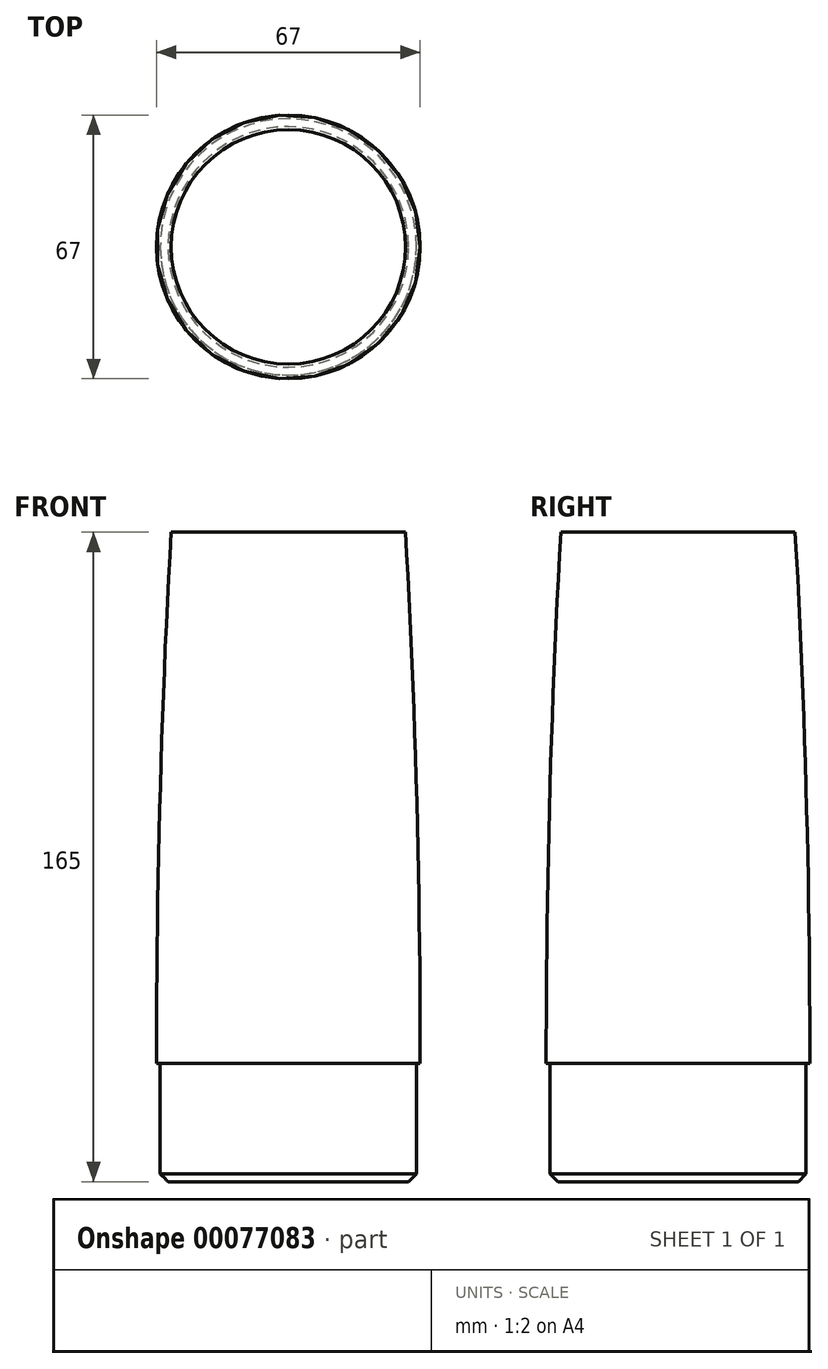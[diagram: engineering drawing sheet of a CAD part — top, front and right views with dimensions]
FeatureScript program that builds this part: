
annotation { "Feature Type Name" : "Feature", "Feature Type Description" : "" }
export const myFeature = defineFeature(function(context is Context, id is Id, definition is map)
    precondition{}
    {
        {
            var Q0;
            Q0=qCreatedBy(makeId("Front.planeOp"),FACE);
            var sketch = newSketch(context, id + "F0", { "sketchPlane" : qUnion([Q0])});
            skEllipticalArc(sketch, "E0", {});
            skLineSegment(sketch, "E1", {"start": v(0, 129) * mm, "end": v(0, -294) * mm, "construction": true});
            skPoint(sketch, "E1.endSnap0", {"position": v(0, 294) * mm});
            skLineSegment(sketch, "E2", {"start": v(-33.5, 0) * mm, "end": v(-32.55, 0) * mm, "construction": true});
            skPoint(sketch, "E2.endSnap0", {"position": v(33.5, 0) * mm});
            skPoint(sketch, "E3.orphan", {"position": v(0, 67.2) * mm});
            skPoint(sketch, "E4.orphan", {"position": v(0, -68.03) * mm});
            skLineSegment(sketch, "E5", {"start": v(-33.5, 0) * mm, "end": v(-32.55, 0) * mm});
            skLineSegment(sketch, "E6", {"start": v(-32.55, 0) * mm, "end": v(-32.55, -30) * mm});
            skLineSegment(sketch, "E7", {"start": v(-32.55, -30) * mm, "end": v(0, -30) * mm});
            skLineSegment(sketch, "E8", {"start": v(0, -30) * mm, "end": v(0, 294) * mm});
            skLineSegment(sketch, "E9.bottom", {"start": v(-32.55, 0) * mm, "end": v(-33.5, 0) * mm});
            skLineSegment(sketch, "E9.top", {"start": v(-25.6, 135) * mm, "end": v(-29.76, 135) * mm});
            skLineSegment(sketch, "E9.left", {"start": v(0, 0) * mm, "end": v(0, 129) * mm});
            skPoint(sketch, "E9.right.end.orphan", {"position": v(-47.64, 135) * mm});
            skPoint(sketch, "E10.orphan", {"position": v(-47.64, 0) * mm});
            skLineSegment(sketch, "E11.trimOffspring", {"start": v(0, 0) * mm, "end": v(40.39, 0) * mm, "construction": true});
            skPoint(sketch, "E12.orphan", {"position": v(-35.36, 0) * mm});
            skPoint(sketch, "E13.orphan", {"position": v(0, 135) * mm});
            skLineSegment(sketch, "E14", {"start": v(-25.6, 135) * mm, "end": v(0, 135) * mm});
            skPoint(sketch, "E15.right.end.orphan", {"position": v(-25.6, 129) * mm});
            const initialGuessF0  = {"E0": [0, 0, 0, 1, 0.294, 0.0335, 1.0937202801470427, 1.5707963267948966]};
            skSetInitialGuess(sketch, initialGuessF0);
            skSolve(sketch);
        }
        {
            var Q0;
            Q0=makeQuery(id+"F0.imprint","IMPRINT",FACE,{"disambiguationData":[TD([[makeQuery(id+"F0.imprint","IMPRINT",EDGE,{"derivedFrom":sQuery(id+"F0.wireOp",EDGE,"E0")}),1.0]])]});
            var Q1;
            Q1=sQuery(id+"F0.wireOp",EDGE,"E1");
            revolve(context, id + "F1", {"entities" : qUnion([Q0]), "axis" : qUnion([Q1]), "revolveType" : RevolveType.FULL});
        }
        {
            var Q0;
            Q0=makeQuery(id+"F1.opRevolve","SWEPT_EDGE",EDGE,{"disambiguationData":[OSD([sQuery(id+"F0.wireOp",EDGE,"E6"),sQuery(id+"F0.wireOp",EDGE,"E7")])]});
            chamfer(context, id + "F2", {"entities" : qUnion([Q0]), "width" : 2 * mm, "tangentPropagation" : true});
        }
    });
